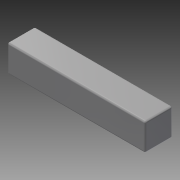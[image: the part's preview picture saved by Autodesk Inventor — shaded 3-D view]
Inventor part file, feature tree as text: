
AUTODESK INVENTOR PART (.ipt)
format: ipt  version: 2018 (Build 220112000, 112)  size: 134,656 bytes
history: native  units: mm (DEFAULTED — no unit token found)
features: other x2, sketch x1, fillet x1
ambient origin geometry x8: Origin, YZ Plane, XZ Plane, XY Plane, X Axis, Y Axis, Z Axis, Center Point
bodies: Solid1 (feature_tree), Body1 (feature_tree)
feature tree (4):
  sketch  "Sketch1"  dims[d1=10.0mm d2=-1.5875mm d3=0.4125mm d4=10.0mm d5=0.0mm d9=0.0mm d10=0.0mm d11=0.0mm d12=0.0mm d13=0.127mm]
  other  "IDS_WORKPLANE{1}"
  other  "IDS_WORKPLANE{2}"
  fillet  "Fillet1"  Radius=1.0mm
